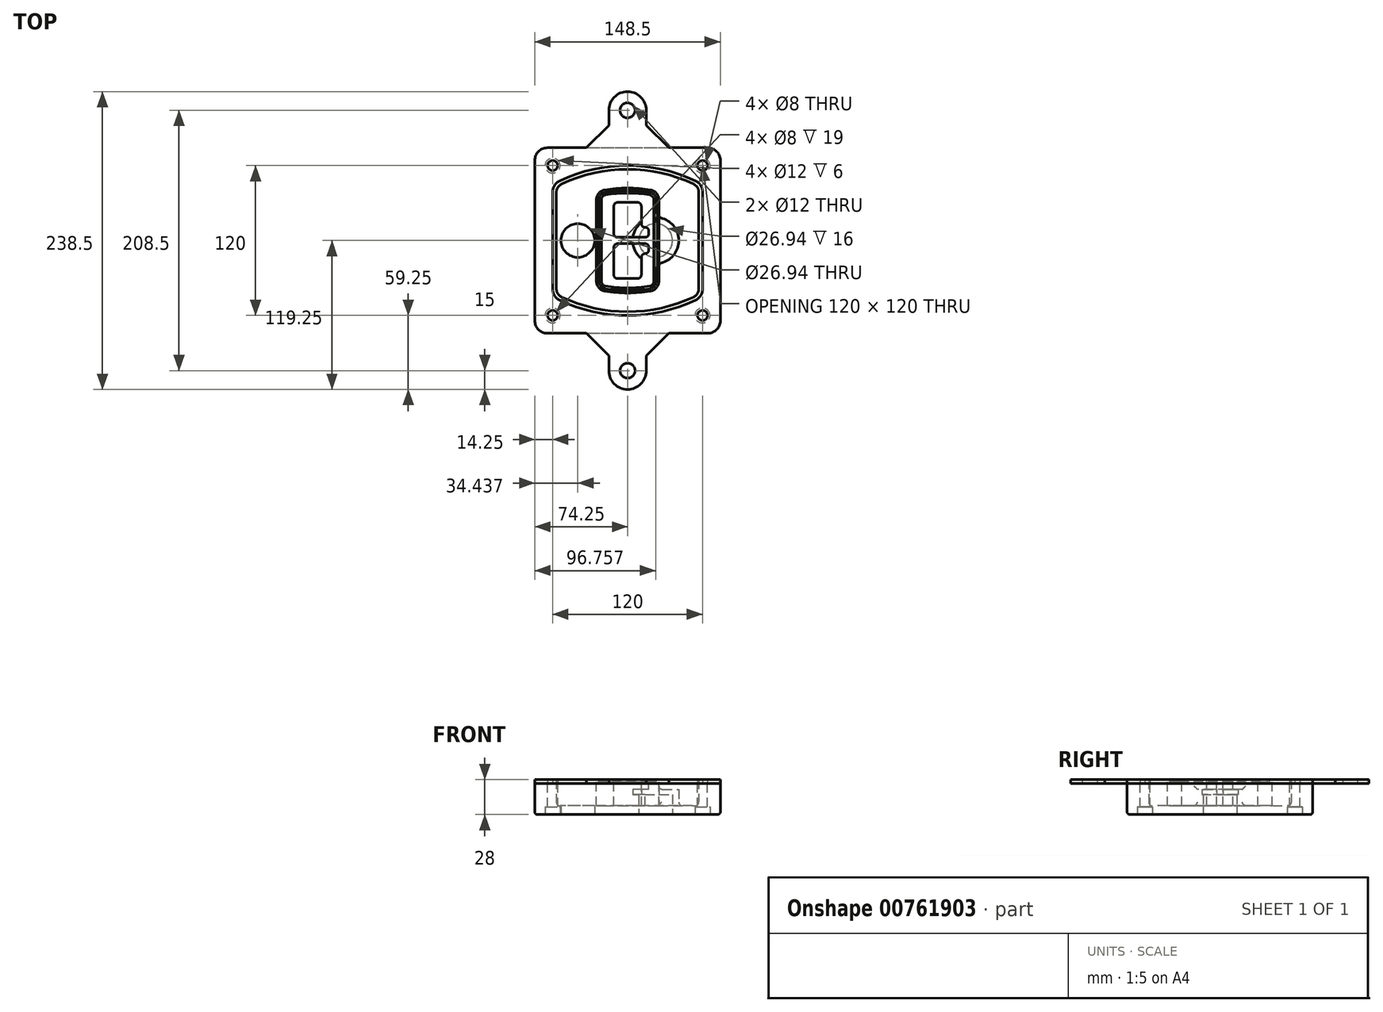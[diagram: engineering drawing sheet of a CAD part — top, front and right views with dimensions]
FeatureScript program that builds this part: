
annotation { "Feature Type Name" : "Feature", "Feature Type Description" : "" }
export const myFeature = defineFeature(function(context is Context, id is Id, definition is map)
    precondition{}
    {
        {
            var Q0;
            Q0=qCreatedBy(makeId("Top.planeOp"),FACE);
            var sketch = newSketch(context, id + "F0", { "sketchPlane" : qUnion([Q0])});
            skPoint(sketch, "E0.rect.middle", {"position": v(0, 0) * mm});
            skLineSegment(sketch, "E1.bottom", {"start": v(-64.25, -74.25) * mm, "end": v(64.25, -74.25) * mm});
            skLineSegment(sketch, "E1.top", {"start": v(-64.25, 74.25) * mm, "end": v(64.25, 74.25) * mm});
            skLineSegment(sketch, "E1.left", {"start": v(-74.25, -64.25) * mm, "end": v(-74.25, 64.25) * mm});
            skLineSegment(sketch, "E1.right", {"start": v(74.25, -64.25) * mm, "end": v(74.25, 64.25) * mm});
            skLineSegment(sketch, "E2", {"start": v(-74.25, 74.25) * mm, "end": v(74.25, -74.25) * mm, "construction": true});
            skLineSegment(sketch, "E3", {"start": v(74.25, 74.25) * mm, "end": v(-74.25, -74.25) * mm, "construction": true});
            skCircle(sketch, "E4", {"center": v(-60, 60) * mm, "radius": 4 * mm});
            skCircle(sketch, "E5", {"center": v(60, 60) * mm, "radius": 4 * mm});
            skCircle(sketch, "E6", {"center": v(60, -60) * mm, "radius": 4 * mm});
            skCircle(sketch, "E7", {"center": v(-60, -60) * mm, "radius": 4 * mm});
            skLineSegment(sketch, "E8", {"start": v(-60, 60) * mm, "end": v(60, 60) * mm, "construction": true});
            skLineSegment(sketch, "E9", {"start": v(60, 60) * mm, "end": v(60, -60) * mm, "construction": true});
            skLineSegment(sketch, "E10", {"start": v(60, -60) * mm, "end": v(-60, -60) * mm, "construction": true});
            skLineSegment(sketch, "E11", {"start": v(-60, -60) * mm, "end": v(-60, 60) * mm, "construction": true});
            skLineSegment(sketch, "E12", {"start": v(-60, 38.83) * mm, "end": v(-60, -38.83) * mm});
            skLineSegment(sketch, "E13", {"start": v(60, 38.83) * mm, "end": v(60, -38.83) * mm});
            skArc(sketch, "E14", {"start": v(54.26, 47.88) * mm, "mid": v(0, 60) * mm, "end": v(-54.26, 47.88) * mm});
            skArc(sketch, "E15", {"start": v(-54.26, -47.88) * mm, "mid": v(0, -60) * mm, "end": v(54.26, -47.88) * mm});
            skLineSegment(sketch, "E16", {"start": v(-60, 0) * mm, "end": v(60, 0) * mm, "construction": true});
            skPoint(sketch, "E17.visualSharp", {"position": v(-60, -45) * mm});
            skArc(sketch, "E17.filletArc", {"start": v(-60, -38.83) * mm, "mid": v(-58.44, -44.2) * mm, "end": v(-54.26, -47.88) * mm});
            skPoint(sketch, "E18.visualSharp", {"position": v(-60, 45) * mm});
            skArc(sketch, "E18.filletArc", {"start": v(-54.26, 47.88) * mm, "mid": v(-58.44, 44.2) * mm, "end": v(-60, 38.83) * mm});
            skPoint(sketch, "E19.visualSharp", {"position": v(60, 45) * mm});
            skArc(sketch, "E19.filletArc", {"start": v(60, 38.83) * mm, "mid": v(58.44, 44.2) * mm, "end": v(54.26, 47.88) * mm});
            skPoint(sketch, "E20.visualSharp", {"position": v(60, -45) * mm});
            skArc(sketch, "E20.filletArc", {"start": v(54.26, -47.88) * mm, "mid": v(58.44, -44.2) * mm, "end": v(60, -38.83) * mm});
            skPoint(sketch, "E21.visualSharp", {"position": v(-74.25, 74.25) * mm});
            skArc(sketch, "E21.filletArc", {"start": v(-64.25, 74.25) * mm, "mid": v(-71.32, 71.32) * mm, "end": v(-74.25, 64.25) * mm});
            skPoint(sketch, "E22.visualSharp", {"position": v(74.25, 74.25) * mm});
            skArc(sketch, "E22.filletArc", {"start": v(74.25, 64.25) * mm, "mid": v(71.32, 71.32) * mm, "end": v(64.25, 74.25) * mm});
            skPoint(sketch, "E23.visualSharp", {"position": v(74.25, -74.25) * mm});
            skArc(sketch, "E23.filletArc", {"start": v(64.25, -74.25) * mm, "mid": v(71.32, -71.32) * mm, "end": v(74.25, -64.25) * mm});
            skPoint(sketch, "E24.visualSharp", {"position": v(-74.25, -74.25) * mm});
            skArc(sketch, "E24.filletArc", {"start": v(-74.25, -64.25) * mm, "mid": v(-71.32, -71.32) * mm, "end": v(-64.25, -74.25) * mm});
            skArc(sketch, "E25.0", {"start": v(57, 38.83) * mm, "mid": v(55.9, 42.58) * mm, "end": v(52.98, 45.17) * mm});
            skLineSegment(sketch, "E25.1", {"start": v(57, 38.83) * mm, "end": v(57, -38.83) * mm});
            skArc(sketch, "E25.2", {"start": v(52.98, -45.17) * mm, "mid": v(55.9, -42.58) * mm, "end": v(57, -38.83) * mm});
            skArc(sketch, "E25.3", {"start": v(-52.98, -45.17) * mm, "mid": v(0, -57) * mm, "end": v(52.98, -45.17) * mm});
            skArc(sketch, "E25.4", {"start": v(-57, -38.83) * mm, "mid": v(-55.9, -42.58) * mm, "end": v(-52.98, -45.17) * mm});
            skArc(sketch, "E25.5", {"start": v(52.98, 45.17) * mm, "mid": v(0, 57) * mm, "end": v(-52.98, 45.17) * mm});
            skLineSegment(sketch, "E25.6", {"start": v(-57, 38.83) * mm, "end": v(-57, -38.83) * mm});
            skArc(sketch, "E25.7", {"start": v(-52.98, 45.17) * mm, "mid": v(-55.9, 42.58) * mm, "end": v(-57, 38.83) * mm});
            skArc(sketch, "E26.0", {"start": v(-55.96, 51.5) * mm, "mid": v(-61.82, 46.33) * mm, "end": v(-64, 38.83) * mm});
            skArc(sketch, "E26.1", {"start": v(55.96, 51.5) * mm, "mid": v(0, 64) * mm, "end": v(-55.96, 51.5) * mm});
            skArc(sketch, "E26.2", {"start": v(64, 38.83) * mm, "mid": v(61.82, 46.33) * mm, "end": v(55.96, 51.5) * mm});
            skLineSegment(sketch, "E26.3", {"start": v(64, 38.83) * mm, "end": v(64, -38.83) * mm});
            skArc(sketch, "E26.4", {"start": v(55.96, -51.5) * mm, "mid": v(61.82, -46.33) * mm, "end": v(64, -38.83) * mm});
            skLineSegment(sketch, "E26.5", {"start": v(-64, 38.83) * mm, "end": v(-64, -38.83) * mm});
            skArc(sketch, "E26.6", {"start": v(-55.96, -51.5) * mm, "mid": v(0, -64) * mm, "end": v(55.96, -51.5) * mm});
            skArc(sketch, "E26.7", {"start": v(-64, -38.83) * mm, "mid": v(-61.82, -46.33) * mm, "end": v(-55.96, -51.5) * mm});
            skSolve(sketch);
        }
        {
            var Q0;
            Q0=makeQuery(id+"F0.imprint","IMPRINT",FACE,{"disambiguationData":[TD([[makeQuery(id+"F0.imprint","IMPRINT",EDGE,{"derivedFrom":sQuery(id+"F0.wireOp",EDGE,"E1.bottom")}),1.0]])]});
            var Q1;
            Q1=makeQuery(id+"F0.imprint","IMPRINT",FACE,{"disambiguationData":[TD([[makeQuery(id+"F0.imprint","IMPRINT",EDGE,{"derivedFrom":sQuery(id+"F0.wireOp",EDGE,"E12")}),1.0]])]});
            var Q2;
            Q2=makeQuery(id+"F0.imprint","IMPRINT",FACE,{"disambiguationData":[TD([[makeQuery(id+"F0.imprint","IMPRINT",EDGE,{"derivedFrom":sQuery(id+"F0.wireOp",EDGE,"E25.0")}),1.0]])]});
            var Q3;
            Q3=makeQuery(id+"F0.imprint","IMPRINT",FACE,{"disambiguationData":[TD([[makeQuery(id+"F0.imprint","IMPRINT",EDGE,{"derivedFrom":sQuery(id+"F0.wireOp",EDGE,"E12")}),-1.0]])]});
            extrude(context, id + "F1", {"entities" : qUnion([Q0, Q1, Q2, Q3]), "oppositeDirection" : true, "depth" : 25 * mm});
        }
        {
            var Q0;
            Q0=makeQuery(id+"F0.imprint","IMPRINT",FACE,{"disambiguationData":[TD([[makeQuery(id+"F0.imprint","IMPRINT",EDGE,{"derivedFrom":sQuery(id+"F0.wireOp",EDGE,"E12")}),1.0]])]});
            extrude(context, id + "F2", {"entities" : qUnion([Q0]), "operationType" : NewBodyOperationType.ADD, "depth" : 3 * mm});
        }
        {
            var Q0;
            Q0=makeQuery(id+"F0.imprint","IMPRINT",FACE,{"disambiguationData":[TD([[makeQuery(id+"F0.imprint","IMPRINT",EDGE,{"derivedFrom":sQuery(id+"F0.wireOp",EDGE,"E25.0")}),1.0]])]});
            extrude(context, id + "F3", {"entities" : qUnion([Q0]), "operationType" : NewBodyOperationType.REMOVE, "oppositeDirection" : true, "depth" : 18 * mm});
        }
        {
            var Q0;
            Q0=makeQuery(id+"F2.opExtrude","CAP_FACE",FACE,{"disambiguationData":[OSD([sQuery(id+"F0.wireOp",EDGE,"E12"),sQuery(id+"F0.wireOp",EDGE,"E13"),sQuery(id+"F0.wireOp",EDGE,"E14"),sQuery(id+"F0.wireOp",EDGE,"E15"),sQuery(id+"F0.wireOp",EDGE,"E17.filletArc"),sQuery(id+"F0.wireOp",EDGE,"E18.filletArc"),sQuery(id+"F0.wireOp",EDGE,"E19.filletArc"),sQuery(id+"F0.wireOp",EDGE,"E20.filletArc"),sQuery(id+"F0.wireOp",EDGE,"E25.0"),sQuery(id+"F0.wireOp",EDGE,"E25.1"),sQuery(id+"F0.wireOp",EDGE,"E25.2"),sQuery(id+"F0.wireOp",EDGE,"E25.3"),sQuery(id+"F0.wireOp",EDGE,"E25.4"),sQuery(id+"F0.wireOp",EDGE,"E25.5"),sQuery(id+"F0.wireOp",EDGE,"E25.6"),sQuery(id+"F0.wireOp",EDGE,"E25.7")])],"isStart":false});
            var sketch = newSketch(context, id + "F4", { "sketchPlane" : qUnion([Q0])});
            skArc(sketch, "E27.0", {"start": v(-18.34, -40.45) * mm, "mid": v(0, -42) * mm, "end": v(18.34, -40.45) * mm});
            skArc(sketch, "E28.0", {"start": v(18.34, 40.45) * mm, "mid": v(0, 42) * mm, "end": v(-18.34, 40.45) * mm});
            skLineSegment(sketch, "E29", {"start": v(-25, 32.57) * mm, "end": v(-25, -32.57) * mm});
            skLineSegment(sketch, "E30", {"start": v(25, 32.57) * mm, "end": v(25, -32.57) * mm});
            skLineSegment(sketch, "E31", {"start": v(-25, 39.1) * mm, "end": v(25, 39.1) * mm, "construction": true});
            skLineSegment(sketch, "E32", {"start": v(-25, -39.1) * mm, "end": v(25, -39.1) * mm, "construction": true});
            skPoint(sketch, "E33.visualSharp", {"position": v(-25, 39.1) * mm});
            skArc(sketch, "E33.filletArc", {"start": v(-18.34, 40.45) * mm, "mid": v(-23.11, 37.73) * mm, "end": v(-25, 32.57) * mm});
            skPoint(sketch, "E34.visualSharp", {"position": v(25, 39.1) * mm});
            skArc(sketch, "E34.filletArc", {"start": v(25, 32.57) * mm, "mid": v(23.11, 37.73) * mm, "end": v(18.34, 40.45) * mm});
            skPoint(sketch, "E35.visualSharp", {"position": v(25, -39.1) * mm});
            skArc(sketch, "E35.filletArc", {"start": v(18.34, -40.45) * mm, "mid": v(23.11, -37.73) * mm, "end": v(25, -32.57) * mm});
            skPoint(sketch, "E36.visualSharp", {"position": v(-25, -39.1) * mm});
            skArc(sketch, "E36.filletArc", {"start": v(-25, -32.57) * mm, "mid": v(-23.11, -37.73) * mm, "end": v(-18.34, -40.45) * mm});
            skArc(sketch, "E37.0", {"start": v(52.98, 45.17) * mm, "mid": v(0, 57) * mm, "end": v(-52.98, 45.17) * mm});
            skArc(sketch, "E37.1", {"start": v(-52.98, 45.17) * mm, "mid": v(-55.9, 42.58) * mm, "end": v(-57, 38.83) * mm});
            skLineSegment(sketch, "E37.2", {"start": v(-57, 38.83) * mm, "end": v(-57, -38.83) * mm});
            skArc(sketch, "E37.3", {"start": v(-57, -38.83) * mm, "mid": v(-55.9, -42.58) * mm, "end": v(-52.98, -45.17) * mm});
            skArc(sketch, "E37.4", {"start": v(-52.98, -45.17) * mm, "mid": v(0, -57) * mm, "end": v(52.98, -45.17) * mm});
            skArc(sketch, "E37.5", {"start": v(52.98, -45.17) * mm, "mid": v(55.9, -42.58) * mm, "end": v(57, -38.83) * mm});
            skLineSegment(sketch, "E37.6", {"start": v(57, 38.83) * mm, "end": v(57, -38.83) * mm});
            skArc(sketch, "E37.7", {"start": v(57, 38.83) * mm, "mid": v(55.9, 42.58) * mm, "end": v(52.98, 45.17) * mm});
            skLineSegment(sketch, "E38.0", {"start": v(23, 32.57) * mm, "end": v(23, -32.57) * mm});
            skArc(sketch, "E38.1", {"start": v(18, -38.48) * mm, "mid": v(21.58, -36.44) * mm, "end": v(23, -32.57) * mm});
            skArc(sketch, "E38.2", {"start": v(-18, -38.48) * mm, "mid": v(0, -40) * mm, "end": v(18, -38.48) * mm});
            skArc(sketch, "E38.3", {"start": v(-23, -32.57) * mm, "mid": v(-21.58, -36.44) * mm, "end": v(-18, -38.48) * mm});
            skLineSegment(sketch, "E38.4", {"start": v(-23, 32.57) * mm, "end": v(-23, -32.57) * mm});
            skArc(sketch, "E38.5", {"start": v(23, 32.57) * mm, "mid": v(21.58, 36.44) * mm, "end": v(18, 38.48) * mm});
            skArc(sketch, "E38.6", {"start": v(-18, 38.48) * mm, "mid": v(-21.58, 36.44) * mm, "end": v(-23, 32.57) * mm});
            skArc(sketch, "E38.7", {"start": v(18, 38.48) * mm, "mid": v(0, 40) * mm, "end": v(-18, 38.48) * mm});
            skArc(sketch, "E39.0", {"start": v(21, 32.57) * mm, "mid": v(20.06, 35.15) * mm, "end": v(17.67, 36.5) * mm});
            skLineSegment(sketch, "E39.1", {"start": v(21, 32.57) * mm, "end": v(21, -32.57) * mm});
            skArc(sketch, "E39.2", {"start": v(17.67, -36.5) * mm, "mid": v(20.06, -35.15) * mm, "end": v(21, -32.57) * mm});
            skArc(sketch, "E39.3", {"start": v(-17.67, -36.5) * mm, "mid": v(0, -38) * mm, "end": v(17.67, -36.5) * mm});
            skArc(sketch, "E39.4", {"start": v(-21, -32.57) * mm, "mid": v(-20.06, -35.15) * mm, "end": v(-17.67, -36.5) * mm});
            skArc(sketch, "E39.5", {"start": v(17.67, 36.5) * mm, "mid": v(0, 38) * mm, "end": v(-17.67, 36.5) * mm});
            skLineSegment(sketch, "E39.6", {"start": v(-21, 32.57) * mm, "end": v(-21, -32.57) * mm});
            skArc(sketch, "E39.7", {"start": v(-17.67, 36.5) * mm, "mid": v(-20.06, 35.15) * mm, "end": v(-21, 32.57) * mm});
            skLineSegment(sketch, "E40", {"start": v(-25, 0) * mm, "end": v(25, 0) * mm, "construction": true});
            skLineSegment(sketch, "E41", {"start": v(-11, 5.5) * mm, "end": v(-11, 27.5) * mm});
            skLineSegment(sketch, "E42", {"start": v(-8, 30.5) * mm, "end": v(8, 30.5) * mm});
            skLineSegment(sketch, "E43", {"start": v(11, 27.5) * mm, "end": v(11, 13.5) * mm});
            skLineSegment(sketch, "E44", {"start": v(14, 10.5) * mm, "end": v(14, 10.5) * mm});
            skLineSegment(sketch, "E45", {"start": v(17, 7.5) * mm, "end": v(17, 5.5) * mm});
            skLineSegment(sketch, "E46", {"start": v(14, 2.5) * mm, "end": v(-8, 2.5) * mm});
            skPoint(sketch, "E47.visualSharp", {"position": v(-11, 30.5) * mm});
            skArc(sketch, "E47.filletArc", {"start": v(-8, 30.5) * mm, "mid": v(-10.12, 29.62) * mm, "end": v(-11, 27.5) * mm});
            skPoint(sketch, "E48.visualSharp", {"position": v(11, 30.5) * mm});
            skArc(sketch, "E48.filletArc", {"start": v(11, 27.5) * mm, "mid": v(10.12, 29.62) * mm, "end": v(8, 30.5) * mm});
            skPoint(sketch, "E49.visualSharp", {"position": v(11, 10.5) * mm});
            skArc(sketch, "E49.filletArc", {"start": v(11, 13.5) * mm, "mid": v(11.88, 11.38) * mm, "end": v(14, 10.5) * mm});
            skPoint(sketch, "E50.visualSharp", {"position": v(17, 10.5) * mm});
            skArc(sketch, "E50.filletArc", {"start": v(17, 7.5) * mm, "mid": v(16.12, 9.62) * mm, "end": v(14, 10.5) * mm});
            skPoint(sketch, "E51.visualSharp", {"position": v(17, 2.5) * mm});
            skArc(sketch, "E51.filletArc", {"start": v(14, 2.5) * mm, "mid": v(16.12, 3.38) * mm, "end": v(17, 5.5) * mm});
            skPoint(sketch, "E52.visualSharp", {"position": v(-11, 2.5) * mm});
            skArc(sketch, "E52.filletArc", {"start": v(-11, 5.5) * mm, "mid": v(-10.12, 3.38) * mm, "end": v(-8, 2.5) * mm});
            skLineSegment(sketch, "E53.0.MirrorCS", {"start": v(14, -2.5) * mm, "end": v(-8, -2.5) * mm});
            skArc(sketch, "E54.0.MirrorCS", {"start": v(-11, -5.5) * mm, "mid": v(-10.12, -3.38) * mm, "end": v(-8, -2.5) * mm});
            skLineSegment(sketch, "E55.0.MirrorCS", {"start": v(-11, -5.5) * mm, "end": v(-11, -27.5) * mm});
            skArc(sketch, "E56.0.MirrorCS", {"start": v(-8, -30.5) * mm, "mid": v(-10.12, -29.62) * mm, "end": v(-11, -27.5) * mm});
            skLineSegment(sketch, "E57.0.MirrorCS", {"start": v(-8, -30.5) * mm, "end": v(8, -30.5) * mm});
            skArc(sketch, "E58.0.MirrorCS", {"start": v(11, -27.5) * mm, "mid": v(10.12, -29.62) * mm, "end": v(8, -30.5) * mm});
            skLineSegment(sketch, "E59.0.MirrorCS", {"start": v(11, -27.5) * mm, "end": v(11, -13.5) * mm});
            skArc(sketch, "E60.0.MirrorCS", {"start": v(11, -13.5) * mm, "mid": v(11.88, -11.38) * mm, "end": v(14, -10.5) * mm});
            skArc(sketch, "E61.0.MirrorCS", {"start": v(17, -7.5) * mm, "mid": v(16.12, -9.62) * mm, "end": v(14, -10.5) * mm});
            skLineSegment(sketch, "E62.0.MirrorCS", {"start": v(17, -7.5) * mm, "end": v(17, -5.5) * mm});
            skArc(sketch, "E63.0.MirrorCS", {"start": v(14, -2.5) * mm, "mid": v(16.12, -3.38) * mm, "end": v(17, -5.5) * mm});
            skSolve(sketch);
        }
        {
            var Q0;
            Q0=makeQuery(id+"F4.imprint","IMPRINT",FACE,{"disambiguationData":[TD([[makeQuery(id+"F4.imprint","IMPRINT",EDGE,{"derivedFrom":sQuery(id+"F4.wireOp",EDGE,"E27.0")}),1.0]])]});
            var Q1;
            Q1=makeQuery(id+"F4.imprint","IMPRINT",FACE,{"disambiguationData":[TD([[makeQuery(id+"F4.imprint","IMPRINT",EDGE,{"derivedFrom":sQuery(id+"F4.wireOp",EDGE,"E38.0")}),-1.0]])]});
            var Q2;
            Q2=makeQuery(id+"F4.imprint","IMPRINT",FACE,{"disambiguationData":[TD([[makeQuery(id+"F4.imprint","IMPRINT",EDGE,{"derivedFrom":sQuery(id+"F4.wireOp",EDGE,"E39.0")}),1.0]])]});
            extrude(context, id + "F5", {"entities" : qUnion([Q0, Q1, Q2]), "operationType" : NewBodyOperationType.ADD, "endBound" : BoundingType.UP_TO_NEXT, "oppositeDirection" : true, "depth" : 25 * mm});
        }
        {
            var Q0;
            Q0=makeQuery(id+"F4.imprint","IMPRINT",FACE,{"disambiguationData":[TD([[makeQuery(id+"F4.imprint","IMPRINT",EDGE,{"derivedFrom":sQuery(id+"F4.wireOp",EDGE,"E38.0")}),-1.0]])]});
            extrude(context, id + "F6", {"entities" : qUnion([Q0]), "operationType" : NewBodyOperationType.REMOVE, "oppositeDirection" : true, "depth" : 2 * mm});
        }
        {
            var Q0;
            Q0=makeQuery(id+"F1.opExtrude","CAP_FACE",FACE,{"disambiguationData":[OSD([sQuery(id+"F0.wireOp",EDGE,"E1.bottom"),sQuery(id+"F0.wireOp",EDGE,"E1.top"),sQuery(id+"F0.wireOp",EDGE,"E1.left"),sQuery(id+"F0.wireOp",EDGE,"E1.right"),sQuery(id+"F0.wireOp",EDGE,"E4"),sQuery(id+"F0.wireOp",EDGE,"E5"),sQuery(id+"F0.wireOp",EDGE,"E6"),sQuery(id+"F0.wireOp",EDGE,"E7"),sQuery(id+"F0.wireOp",EDGE,"E21.filletArc"),sQuery(id+"F0.wireOp",EDGE,"E22.filletArc"),sQuery(id+"F0.wireOp",EDGE,"E23.filletArc"),sQuery(id+"F0.wireOp",EDGE,"E24.filletArc")])],"isStart":false});
            var sketch = newSketch(context, id + "F7", { "sketchPlane" : qUnion([Q0])});
            skCircle(sketch, "E64", {"center": v(22.5, 0) * mm, "radius": 13.47 * mm});
            skCircle(sketch, "E65", {"center": v(-39.81, 0) * mm, "radius": 13.47 * mm});
            skLineSegment(sketch, "E66", {"start": v(74.25, 0) * mm, "end": v(-74.25, 0) * mm});
            skCircle(sketch, "E67", {"center": v(22.5, 0) * mm, "radius": 18.47 * mm});
            skCircle(sketch, "E68", {"center": v(60, -60) * mm, "radius": 6 * mm});
            skCircle(sketch, "E69", {"center": v(-60, -60) * mm, "radius": 6 * mm});
            skCircle(sketch, "E70", {"center": v(-60, 60) * mm, "radius": 6 * mm});
            skCircle(sketch, "E71", {"center": v(60, 60) * mm, "radius": 6 * mm});
            skSolve(sketch);
        }
        {
            var Q0;
            {var subQ1=sQuery(id+"F7.wireOp",EDGE,"E66");var subQ4=sQuery(id+"F7.wireOp",EDGE,"E64");var subQ6=makeQuery(id+"F7.imprint","INTERSECT",VERTEX,{"disambiguationData":[OD(0.0)],"derivedFrom":[subQ4,subQ1]});Q0=makeQuery(id+"F7.imprint","IMPRINT",FACE,{"disambiguationData":[TD([[makeQuery(id+"F7.imprint","IMPRINT",EDGE,{"disambiguationData":[TD([[subQ6,-1.0]])],"derivedFrom":subQ4}),-1.0]])]});}
            var Q1;
            {var subQ0=sQuery(id+"F7.wireOp",EDGE,"E66");var subQ1=sQuery(id+"F7.wireOp",EDGE,"E64");var subQ3=makeQuery(id+"F7.imprint","INTERSECT",VERTEX,{"disambiguationData":[OD(0.0)],"derivedFrom":[subQ1,subQ0]});Q1=makeQuery(id+"F7.imprint","IMPRINT",FACE,{"disambiguationData":[TD([[makeQuery(id+"F7.imprint","IMPRINT",EDGE,{"disambiguationData":[TD([[subQ3,-1.0]])],"derivedFrom":subQ1}),1.0]])]});}
            var Q2;
            {var subQ0=sQuery(id+"F7.wireOp",EDGE,"E66");var subQ1=sQuery(id+"F7.wireOp",EDGE,"E64");var subQ3=makeQuery(id+"F7.imprint","INTERSECT",VERTEX,{"disambiguationData":[OD(0.0)],"derivedFrom":[subQ1,subQ0]});Q2=makeQuery(id+"F7.imprint","IMPRINT",FACE,{"disambiguationData":[TD([[makeQuery(id+"F7.imprint","IMPRINT",EDGE,{"disambiguationData":[TD([[subQ3,1.0]])],"derivedFrom":subQ1}),1.0]])]});}
            var Q3;
            {var subQ1=sQuery(id+"F7.wireOp",EDGE,"E66");var subQ4=sQuery(id+"F7.wireOp",EDGE,"E64");var subQ6=makeQuery(id+"F7.imprint","INTERSECT",VERTEX,{"disambiguationData":[OD(0.0)],"derivedFrom":[subQ4,subQ1]});Q3=makeQuery(id+"F7.imprint","IMPRINT",FACE,{"disambiguationData":[TD([[makeQuery(id+"F7.imprint","IMPRINT",EDGE,{"disambiguationData":[TD([[subQ6,1.0]])],"derivedFrom":subQ4}),-1.0]])]});}
            extrude(context, id + "F8", {"entities" : qUnion([Q0, Q1, Q2, Q3]), "operationType" : NewBodyOperationType.ADD, "oppositeDirection" : true, "depth" : 20 * mm});
        }
        {
            var Q0;
            {var subQ0=sQuery(id+"F7.wireOp",EDGE,"E66");var subQ1=sQuery(id+"F7.wireOp",EDGE,"E64");var subQ3=makeQuery(id+"F7.imprint","INTERSECT",VERTEX,{"disambiguationData":[OD(0.0)],"derivedFrom":[subQ1,subQ0]});Q0=makeQuery(id+"F7.imprint","IMPRINT",FACE,{"disambiguationData":[TD([[makeQuery(id+"F7.imprint","IMPRINT",EDGE,{"disambiguationData":[TD([[subQ3,-1.0]])],"derivedFrom":subQ1}),1.0]])]});}
            var Q1;
            {var subQ0=sQuery(id+"F7.wireOp",EDGE,"E66");var subQ1=sQuery(id+"F7.wireOp",EDGE,"E64");var subQ3=makeQuery(id+"F7.imprint","INTERSECT",VERTEX,{"disambiguationData":[OD(0.0)],"derivedFrom":[subQ1,subQ0]});Q1=makeQuery(id+"F7.imprint","IMPRINT",FACE,{"disambiguationData":[TD([[makeQuery(id+"F7.imprint","IMPRINT",EDGE,{"disambiguationData":[TD([[subQ3,1.0]])],"derivedFrom":subQ1}),1.0]])]});}
            extrude(context, id + "F9", {"entities" : qUnion([Q0, Q1]), "operationType" : NewBodyOperationType.REMOVE, "oppositeDirection" : true, "depth" : 16 * mm});
        }
        {
            var Q0;
            {var subQ0=sQuery(id+"F7.wireOp",EDGE,"E66");var subQ1=sQuery(id+"F7.wireOp",EDGE,"E65");var subQ3=makeQuery(id+"F7.imprint","INTERSECT",VERTEX,{"disambiguationData":[OD(0.0)],"derivedFrom":[subQ1,subQ0]});Q0=makeQuery(id+"F7.imprint","IMPRINT",FACE,{"disambiguationData":[TD([[makeQuery(id+"F7.imprint","IMPRINT",EDGE,{"disambiguationData":[TD([[subQ3,-1.0]])],"derivedFrom":subQ1}),1.0]])]});}
            var Q1;
            {var subQ0=sQuery(id+"F7.wireOp",EDGE,"E66");var subQ1=sQuery(id+"F7.wireOp",EDGE,"E65");var subQ3=makeQuery(id+"F7.imprint","INTERSECT",VERTEX,{"disambiguationData":[OD(0.0)],"derivedFrom":[subQ1,subQ0]});Q1=makeQuery(id+"F7.imprint","IMPRINT",FACE,{"disambiguationData":[TD([[makeQuery(id+"F7.imprint","IMPRINT",EDGE,{"disambiguationData":[TD([[subQ3,1.0]])],"derivedFrom":subQ1}),1.0]])]});}
            extrude(context, id + "F10", {"entities" : qUnion([Q0, Q1]), "operationType" : NewBodyOperationType.REMOVE, "oppositeDirection" : true, "depth" : 25 * mm});
        }
        {
            var Q0;
            Q0=makeQuery(id+"F7.imprint","IMPRINT",FACE,{"disambiguationData":[TD([[makeQuery(id+"F7.imprint","IMPRINT",EDGE,{"derivedFrom":sQuery(id+"F7.wireOp",EDGE,"E68")}),1.0]])]});
            var Q1;
            Q1=makeQuery(id+"F7.imprint","IMPRINT",FACE,{"disambiguationData":[TD([[makeQuery(id+"F7.imprint","IMPRINT",EDGE,{"derivedFrom":makeQuery(id+"F1.opExtrude","CAP_EDGE",EDGE,{"disambiguationData":[OSD([sQuery(id+"F0.wireOp",EDGE,"E5")])],"isStart":false})}),-1.0]])]});
            var Q2;
            Q2=makeQuery(id+"F7.imprint","IMPRINT",FACE,{"disambiguationData":[TD([[makeQuery(id+"F7.imprint","IMPRINT",EDGE,{"derivedFrom":sQuery(id+"F7.wireOp",EDGE,"E69")}),1.0]])]});
            var Q3;
            Q3=makeQuery(id+"F7.imprint","IMPRINT",FACE,{"disambiguationData":[TD([[makeQuery(id+"F7.imprint","IMPRINT",EDGE,{"derivedFrom":makeQuery(id+"F1.opExtrude","CAP_EDGE",EDGE,{"disambiguationData":[OSD([sQuery(id+"F0.wireOp",EDGE,"E4")])],"isStart":false})}),-1.0]])]});
            var Q4;
            Q4=makeQuery(id+"F7.imprint","IMPRINT",FACE,{"disambiguationData":[TD([[makeQuery(id+"F7.imprint","IMPRINT",EDGE,{"derivedFrom":sQuery(id+"F7.wireOp",EDGE,"E70")}),1.0]])]});
            var Q5;
            Q5=makeQuery(id+"F7.imprint","IMPRINT",FACE,{"disambiguationData":[TD([[makeQuery(id+"F7.imprint","IMPRINT",EDGE,{"derivedFrom":makeQuery(id+"F1.opExtrude","CAP_EDGE",EDGE,{"disambiguationData":[OSD([sQuery(id+"F0.wireOp",EDGE,"E7")])],"isStart":false})}),-1.0]])]});
            var Q6;
            Q6=makeQuery(id+"F7.imprint","IMPRINT",FACE,{"disambiguationData":[TD([[makeQuery(id+"F7.imprint","IMPRINT",EDGE,{"derivedFrom":sQuery(id+"F7.wireOp",EDGE,"E71")}),1.0]])]});
            var Q7;
            Q7=makeQuery(id+"F7.imprint","IMPRINT",FACE,{"disambiguationData":[TD([[makeQuery(id+"F7.imprint","IMPRINT",EDGE,{"derivedFrom":makeQuery(id+"F1.opExtrude","CAP_EDGE",EDGE,{"disambiguationData":[OSD([sQuery(id+"F0.wireOp",EDGE,"E6")])],"isStart":false})}),-1.0]])]});
            extrude(context, id + "F11", {"entities" : qUnion([Q0, Q1, Q2, Q3, Q4, Q5, Q6, Q7]), "operationType" : NewBodyOperationType.REMOVE, "oppositeDirection" : true, "depth" : 6 * mm});
        }
        {
            var Q0;
            Q0=makeQuery(id+"F9.boolean.opBoolean","COPY",FACE,{"derivedFrom":makeQuery(id+"F9.opExtrude","CAP_FACE",FACE,{"disambiguationData":[OSD([sQuery(id+"F7.wireOp",EDGE,"E64")])],"isStart":false})});
            var sketch = newSketch(context, id + "F12", { "sketchPlane" : qUnion([Q0])});
            skArc(sketch, "E72.0", {"start": v(11, 14.45) * mm, "mid": v(6.45, 9.13) * mm, "end": v(4.2, 2.5) * mm});
            skArc(sketch, "E72.1", {"start": v(4.2, -2.5) * mm, "mid": v(6.45, -9.13) * mm, "end": v(11, -14.45) * mm});
            skLineSegment(sketch, "E73", {"start": v(4.2, -2.5) * mm, "end": v(14, -2.5) * mm});
            skLineSegment(sketch, "E74.0", {"start": v(14, 2.5) * mm, "end": v(4.2, 2.5) * mm});
            skArc(sketch, "E74.1", {"start": v(14, 2.5) * mm, "mid": v(16.12, 3.38) * mm, "end": v(17, 5.5) * mm});
            skLineSegment(sketch, "E74.2", {"start": v(17, 7.5) * mm, "end": v(17, 5.5) * mm});
            skArc(sketch, "E74.3", {"start": v(17, 7.5) * mm, "mid": v(16.12, 9.62) * mm, "end": v(14, 10.5) * mm});
            skArc(sketch, "E74.4", {"start": v(11, 13.5) * mm, "mid": v(11.88, 11.38) * mm, "end": v(14, 10.5) * mm});
            skLineSegment(sketch, "E74.5", {"start": v(11, 14.45) * mm, "end": v(11, 13.5) * mm});
            skLineSegment(sketch, "E74.7", {"start": v(14, -2.5) * mm, "end": v(4.2, -2.5) * mm});
            skArc(sketch, "E74.8", {"start": v(14, -2.5) * mm, "mid": v(16.12, -3.38) * mm, "end": v(17, -5.5) * mm});
            skLineSegment(sketch, "E74.9", {"start": v(17, -7.5) * mm, "end": v(17, -5.5) * mm});
            skArc(sketch, "E74.10", {"start": v(17, -7.5) * mm, "mid": v(16.12, -9.62) * mm, "end": v(14, -10.5) * mm});
            skArc(sketch, "E74.11", {"start": v(11, -13.5) * mm, "mid": v(11.88, -11.38) * mm, "end": v(14, -10.5) * mm});
            skLineSegment(sketch, "E74.12", {"start": v(11, -14.45) * mm, "end": v(11, -13.5) * mm});
            skPoint(sketch, "E75.orphan", {"position": v(11, -27.5) * mm});
            skPoint(sketch, "E76.orphan", {"position": v(-8, -2.5) * mm});
            skPoint(sketch, "E77.orphan", {"position": v(-8, 2.5) * mm});
            skPoint(sketch, "E78.orphan", {"position": v(11, 27.5) * mm});
            skSolve(sketch);
        }
        {
            var Q0;
            {var subQ7=sQuery(id+"F12.wireOp",EDGE,"E72.0");var subQ14=sQuery(id+"F12.wireOp",EDGE,"E72.1");var subQ16=sQuery(id+"F12.wireOp",EDGE,"E74.1");var subQ18=sQuery(id+"F12.wireOp",EDGE,"E74.8");Q0=qUnion([makeQuery(id+"F12.imprint","IMPRINT",FACE,{"disambiguationData":[TD([[makeQuery(id+"F12.imprint","IMPRINT",EDGE,{"derivedFrom":subQ7}),1.0]])]}),makeQuery(id+"F12.imprint","IMPRINT",FACE,{"disambiguationData":[TD([[makeQuery(id+"F12.imprint","IMPRINT",EDGE,{"derivedFrom":subQ14}),1.0]])]}),makeQuery(id+"F12.imprint","IMPRINT",FACE,{"disambiguationData":[TD([[makeQuery(id+"F12.imprint","IMPRINT",EDGE,{"derivedFrom":subQ16}),1.0]])]}),makeQuery(id+"F12.imprint","IMPRINT",FACE,{"disambiguationData":[TD([[makeQuery(id+"F12.imprint","IMPRINT",EDGE,{"derivedFrom":subQ18}),-1.0]])]})]);}
            var Q1;
            Q1=makeQuery(id+"F5.boolean.opBoolean","SPLIT",FACE,{"disambiguationData":[TD([makeQuery(id+"F5.opExtrude","SWEPT_FACE",FACE,{"disambiguationData":[OSD([sQuery(id+"F4.wireOp",EDGE,"E41")])]})])],"derivedFrom":makeQuery(id+"F3.boolean.opBoolean","COPY",FACE,{"derivedFrom":makeQuery(id+"F3.opExtrude","CAP_FACE",FACE,{"disambiguationData":[OSD([sQuery(id+"F0.wireOp",EDGE,"E25.0"),sQuery(id+"F0.wireOp",EDGE,"E25.1"),sQuery(id+"F0.wireOp",EDGE,"E25.2"),sQuery(id+"F0.wireOp",EDGE,"E25.3"),sQuery(id+"F0.wireOp",EDGE,"E25.4"),sQuery(id+"F0.wireOp",EDGE,"E25.5"),sQuery(id+"F0.wireOp",EDGE,"E25.6"),sQuery(id+"F0.wireOp",EDGE,"E25.7")])],"isStart":false})})});
            extrude(context, id + "F13", {"entities" : qUnion([Q0]), "operationType" : NewBodyOperationType.REMOVE, "endBound" : BoundingType.UP_TO_SURFACE, "endBoundEntityFace" : qUnion([Q1]), "depth" : 25 * mm});
        }
        {
            var Q0;
            Q0=makeQuery(id+"F3.boolean.opBoolean","COPY",EDGE,{"derivedFrom":makeQuery(id+"F3.opExtrude","CAP_EDGE",EDGE,{"disambiguationData":[OSD([sQuery(id+"F0.wireOp",EDGE,"E25.6")])],"isStart":false})});
            var Q1;
            Q1=makeQuery(id+"F8.boolean.opBoolean","INTERSECT",EDGE,{"derivedFrom":[makeQuery(id+"F5.opExtrude","SWEPT_FACE",FACE,{"disambiguationData":[OSD([sQuery(id+"F4.wireOp",EDGE,"E30")])]}),makeQuery(id+"F8.opExtrude","CAP_FACE",FACE,{"disambiguationData":[OSD([sQuery(id+"F7.wireOp",EDGE,"E67")])],"isStart":false})]});
            var Q2;
            Q2=makeQuery(id+"F8.boolean.opBoolean","INTERSECT",EDGE,{"disambiguationData":[OD(1.0)],"derivedFrom":[makeQuery(id+"F5.opExtrude","SWEPT_FACE",FACE,{"disambiguationData":[OSD([sQuery(id+"F4.wireOp",EDGE,"E30")])]}),makeQuery(id+"F8.opExtrude","SWEPT_FACE",FACE,{"disambiguationData":[OSD([sQuery(id+"F7.wireOp",EDGE,"E67")])]})]});
            var Q3;
            {var subQ0=sQuery(id+"F4.wireOp",EDGE,"E30");Q3=makeQuery(id+"F8.boolean.opBoolean","SPLIT",EDGE,{"disambiguationData":[TD([makeQuery(id+"F5.opExtrude","SWEPT_FACE",FACE,{"disambiguationData":[OSD([sQuery(id+"F4.wireOp",EDGE,"E35.filletArc")])]})])],"derivedFrom":makeQuery(id+"F5.opExtrude","CAP_EDGE",EDGE,{"disambiguationData":[OSD([subQ0])],"isStart":false})});}
            var Q4;
            {var subQ0=sQuery(id+"F0.wireOp",EDGE,"E25.7");var subQ1=sQuery(id+"F0.wireOp",EDGE,"E25.1");var subQ2=sQuery(id+"F0.wireOp",EDGE,"E25.6");var subQ3=sQuery(id+"F0.wireOp",EDGE,"E25.5");var subQ4=sQuery(id+"F0.wireOp",EDGE,"E25.4");var subQ5=sQuery(id+"F0.wireOp",EDGE,"E25.0");var subQ6=sQuery(id+"F0.wireOp",EDGE,"E25.2");var subQ7=sQuery(id+"F0.wireOp",EDGE,"E25.3");Q4=makeQuery(id+"F8.boolean.opBoolean","INTERSECT",EDGE,{"derivedFrom":[makeQuery(id+"F5.boolean.opBoolean","SPLIT",FACE,{"disambiguationData":[TD([makeQuery(id+"F2.opExtrude","SWEPT_FACE",FACE,{"disambiguationData":[OSD([subQ5])]})])],"derivedFrom":makeQuery(id+"F3.boolean.opBoolean","COPY",FACE,{"derivedFrom":makeQuery(id+"F3.opExtrude","CAP_FACE",FACE,{"disambiguationData":[OSD([subQ5,subQ1,subQ6,subQ7,subQ4,subQ3,subQ2,subQ0])],"isStart":false})})}),makeQuery(id+"F8.opExtrude","SWEPT_FACE",FACE,{"disambiguationData":[OSD([sQuery(id+"F7.wireOp",EDGE,"E67")])]})]});}
            var Q5;
            Q5=makeQuery(id+"F8.boolean.opBoolean","INTERSECT",EDGE,{"disambiguationData":[OD(0.0)],"derivedFrom":[makeQuery(id+"F5.opExtrude","SWEPT_FACE",FACE,{"disambiguationData":[OSD([sQuery(id+"F4.wireOp",EDGE,"E30")])]}),makeQuery(id+"F8.opExtrude","SWEPT_FACE",FACE,{"disambiguationData":[OSD([sQuery(id+"F7.wireOp",EDGE,"E67")])]})]});
            fillet(context, id + "F14", {"entities" : qUnion([Q0, Q1, Q2, Q3, Q4, Q5]), "radius" : 3 * mm, "tangentPropagation" : true, "allowEdgeOverflow" : false});
        }
        {
            var Q0;
            Q0=makeQuery(id+"F1.opExtrude","CAP_EDGE",EDGE,{"disambiguationData":[OSD([sQuery(id+"F0.wireOp",EDGE,"E1.bottom")])],"isStart":false});
            fillet(context, id + "F15", {"entities" : qUnion([Q0]), "radius" : 2 * mm, "tangentPropagation" : true, "allowEdgeOverflow" : false});
        }
        {
            var Q0;
            {var subQ0=sQuery(id+"F0.wireOp",EDGE,"E21.filletArc");var subQ1=sQuery(id+"F0.wireOp",EDGE,"E7");var subQ2=sQuery(id+"F0.wireOp",EDGE,"E6");var subQ3=sQuery(id+"F0.wireOp",EDGE,"E5");var subQ4=sQuery(id+"F0.wireOp",EDGE,"E4");var subQ5=sQuery(id+"F0.wireOp",EDGE,"E22.filletArc");var subQ6=sQuery(id+"F0.wireOp",EDGE,"E1.bottom");var subQ7=sQuery(id+"F0.wireOp",EDGE,"E1.right");var subQ8=sQuery(id+"F0.wireOp",EDGE,"E1.top");var subQ9=sQuery(id+"F0.wireOp",EDGE,"E1.left");var subQ10=sQuery(id+"F0.wireOp",EDGE,"E23.filletArc");var subQ11=sQuery(id+"F0.wireOp",EDGE,"E24.filletArc");Q0=makeQuery(id+"F2.boolean.opBoolean","SPLIT",FACE,{"disambiguationData":[TD([makeQuery(id+"F1.opExtrude","SWEPT_FACE",FACE,{"disambiguationData":[OSD([subQ6])]})])],"derivedFrom":makeQuery(id+"F1.opExtrude","CAP_FACE",FACE,{"disambiguationData":[OSD([subQ6,subQ8,subQ9,subQ7,subQ4,subQ3,subQ2,subQ1,subQ0,subQ5,subQ10,subQ11])],"isStart":true})});}
            var sketch = newSketch(context, id + "F16", { "sketchPlane" : qUnion([Q0])});
            skLineSegment(sketch, "E79.0.0", {"start": v(64.25, 74.25) * mm, "end": v(-64.25, 74.25) * mm});
            skArc(sketch, "E79.0.1", {"start": v(-64.25, 74.25) * mm, "mid": v(-71.32, 71.32) * mm, "end": v(-74.25, 64.25) * mm});
            skLineSegment(sketch, "E79.0.2", {"start": v(-74.25, 64.25) * mm, "end": v(-74.25, -64.25) * mm});
            skArc(sketch, "E79.0.3", {"start": v(-74.25, -64.25) * mm, "mid": v(-71.32, -71.32) * mm, "end": v(-64.25, -74.25) * mm});
            skLineSegment(sketch, "E79.0.4", {"start": v(-64.25, -74.25) * mm, "end": v(64.25, -74.25) * mm});
            skArc(sketch, "E79.0.5", {"start": v(64.25, -74.25) * mm, "mid": v(71.32, -71.32) * mm, "end": v(74.25, -64.25) * mm});
            skLineSegment(sketch, "E79.0.6", {"start": v(74.25, -64.25) * mm, "end": v(74.25, 64.25) * mm});
            skArc(sketch, "E79.0.7", {"start": v(74.25, 64.25) * mm, "mid": v(71.32, 71.32) * mm, "end": v(64.25, 74.25) * mm});
            skCircle(sketch, "E80.0", {"center": v(-60, 60) * mm, "radius": 4 * mm});
            skCircle(sketch, "E81.0", {"center": v(60, 60) * mm, "radius": 4 * mm});
            skCircle(sketch, "E82.0", {"center": v(60, -60) * mm, "radius": 4 * mm});
            skCircle(sketch, "E83.0", {"center": v(-60, -60) * mm, "radius": 4 * mm});
            skLineSegment(sketch, "E84.0", {"start": v(-60, 38.83) * mm, "end": v(-60, -38.83) * mm});
            skArc(sketch, "E85.0", {"start": v(54.26, 47.88) * mm, "mid": v(0, 60) * mm, "end": v(-54.26, 47.88) * mm});
            skArc(sketch, "E86.0", {"start": v(-54.26, 47.88) * mm, "mid": v(-58.44, 44.2) * mm, "end": v(-60, 38.83) * mm});
            skArc(sketch, "E87.0", {"start": v(60, 38.83) * mm, "mid": v(58.44, 44.2) * mm, "end": v(54.26, 47.88) * mm});
            skLineSegment(sketch, "E88.0", {"start": v(60, 38.83) * mm, "end": v(60, -38.83) * mm});
            skArc(sketch, "E89.0", {"start": v(54.26, -47.88) * mm, "mid": v(58.44, -44.2) * mm, "end": v(60, -38.83) * mm});
            skArc(sketch, "E90.0", {"start": v(-54.26, -47.88) * mm, "mid": v(0, -60) * mm, "end": v(54.26, -47.88) * mm});
            skArc(sketch, "E91.0", {"start": v(-60, -38.83) * mm, "mid": v(-58.44, -44.2) * mm, "end": v(-54.26, -47.88) * mm});
            skLineSegment(sketch, "E92", {"start": v(-74.25, 0) * mm, "end": v(74.25, 0) * mm, "construction": true});
            skLineSegment(sketch, "E93", {"start": v(0, 74.25) * mm, "end": v(0, 104.25) * mm});
            skCircle(sketch, "E94", {"center": v(0, 104.25) * mm, "radius": 6 * mm});
            skArc(sketch, "E95", {"start": v(15, 104.25) * mm, "mid": v(0, 119.25) * mm, "end": v(-15, 104.25) * mm});
            skLineSegment(sketch, "E96", {"start": v(-15, 104.25) * mm, "end": v(-15, 92.25) * mm});
            skLineSegment(sketch, "E97", {"start": v(-15, 92.25) * mm, "end": v(-33, 74.25) * mm});
            skLineSegment(sketch, "E98", {"start": v(15, 104.25) * mm, "end": v(15, 92.25) * mm});
            skLineSegment(sketch, "E99", {"start": v(15, 92.25) * mm, "end": v(33, 74.25) * mm});
            skLineSegment(sketch, "E100.MirrorCS", {"start": v(-15, -92.25) * mm, "end": v(-33, -74.25) * mm});
            skLineSegment(sketch, "E101.MirrorCS", {"start": v(-15, -104.25) * mm, "end": v(-15, -92.25) * mm});
            skArc(sketch, "E102.MirrorCS", {"start": v(15, -104.25) * mm, "mid": v(0, -119.25) * mm, "end": v(-15, -104.25) * mm});
            skCircle(sketch, "E103.MirrorC", {"center": v(0, -104.25) * mm, "radius": 6 * mm});
            skLineSegment(sketch, "E104.MirrorCS", {"start": v(0, -74.25) * mm, "end": v(0, -104.25) * mm});
            skLineSegment(sketch, "E105.MirrorCS", {"start": v(15, -104.25) * mm, "end": v(15, -92.25) * mm});
            skLineSegment(sketch, "E106.MirrorCS", {"start": v(15, -92.25) * mm, "end": v(33, -74.25) * mm});
            skSolve(sketch);
        }
        {
            var Q0;
            Q0 = qSketchRegion(id + "F16", true);
            var Q1;
            Q1=makeQuery(id+"F2.opExtrude","CAP_FACE",FACE,{"disambiguationData":[OSD([sQuery(id+"F0.wireOp",EDGE,"E12"),sQuery(id+"F0.wireOp",EDGE,"E13"),sQuery(id+"F0.wireOp",EDGE,"E14"),sQuery(id+"F0.wireOp",EDGE,"E15"),sQuery(id+"F0.wireOp",EDGE,"E17.filletArc"),sQuery(id+"F0.wireOp",EDGE,"E18.filletArc"),sQuery(id+"F0.wireOp",EDGE,"E19.filletArc"),sQuery(id+"F0.wireOp",EDGE,"E20.filletArc"),sQuery(id+"F0.wireOp",EDGE,"E25.0"),sQuery(id+"F0.wireOp",EDGE,"E25.1"),sQuery(id+"F0.wireOp",EDGE,"E25.2"),sQuery(id+"F0.wireOp",EDGE,"E25.3"),sQuery(id+"F0.wireOp",EDGE,"E25.4"),sQuery(id+"F0.wireOp",EDGE,"E25.5"),sQuery(id+"F0.wireOp",EDGE,"E25.6"),sQuery(id+"F0.wireOp",EDGE,"E25.7")])],"isStart":false});
            extrude(context, id + "F17", {"entities" : qUnion([Q0]), "endBound" : BoundingType.UP_TO_SURFACE, "depth" : 25 * mm, "endBoundEntityFace" : qUnion([Q1]), "offsetDistance" : 25 * mm});
        }
    });
